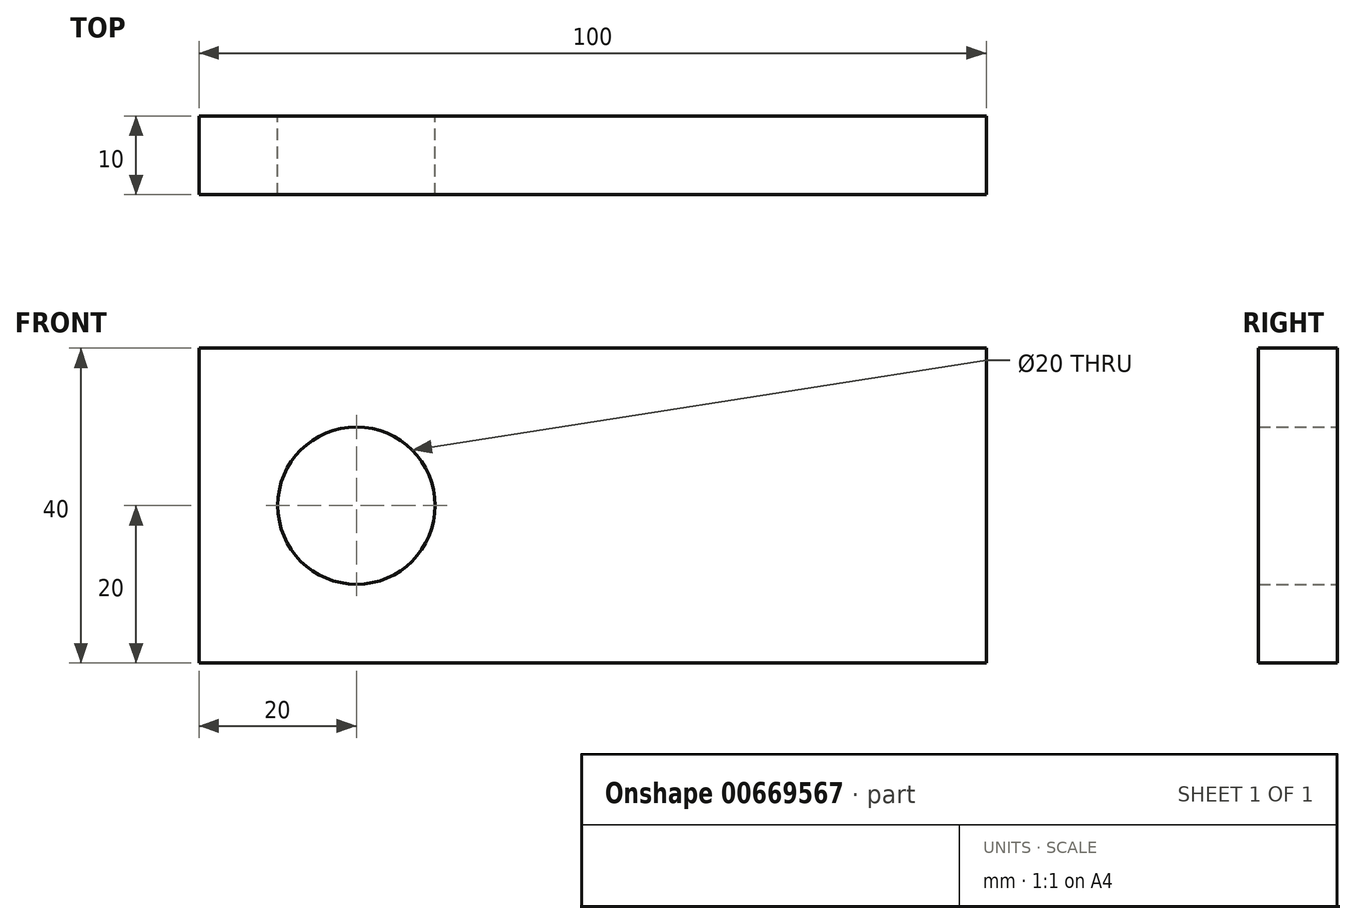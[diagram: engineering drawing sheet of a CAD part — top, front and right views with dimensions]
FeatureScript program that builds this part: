
annotation { "Feature Type Name" : "Feature", "Feature Type Description" : "" }
export const myFeature = defineFeature(function(context is Context, id is Id, definition is map)
    precondition{}
    {
        {
            var Q0;
            Q0=qCreatedBy(makeId("Front.planeOp"),FACE);
            var sketch = newSketch(context, id + "F0", { "sketchPlane" : qUnion([Q0])});
            skLineSegment(sketch, "E0", {"start": v(0, 0) * mm, "end": v(-100, 0) * mm});
            skLineSegment(sketch, "E1", {"start": v(-100, 40) * mm, "end": v(-100, 0) * mm});
            skLineSegment(sketch, "E2", {"start": v(0, 40) * mm, "end": v(0, 0) * mm});
            skLineSegment(sketch, "E3", {"start": v(0, 40) * mm, "end": v(-100, 40) * mm});
            skCircle(sketch, "E4", {"center": v(-80, 20) * mm, "radius": 10 * mm});
            skSolve(sketch);
        }
        {
            var Q0;
            Q0=makeQuery(id+"F0.imprint","IMPRINT",FACE,{"disambiguationData":[TD([[makeQuery(id+"F0.imprint","IMPRINT",EDGE,{"derivedFrom":sQuery(id+"F0.wireOp",EDGE,"E0")}),-1.0]])]});
            extrude(context, id + "F1", {"entities" : qUnion([Q0]), "depth" : 10 * mm, "offsetDistance" : 25 * mm});
        }
    });
